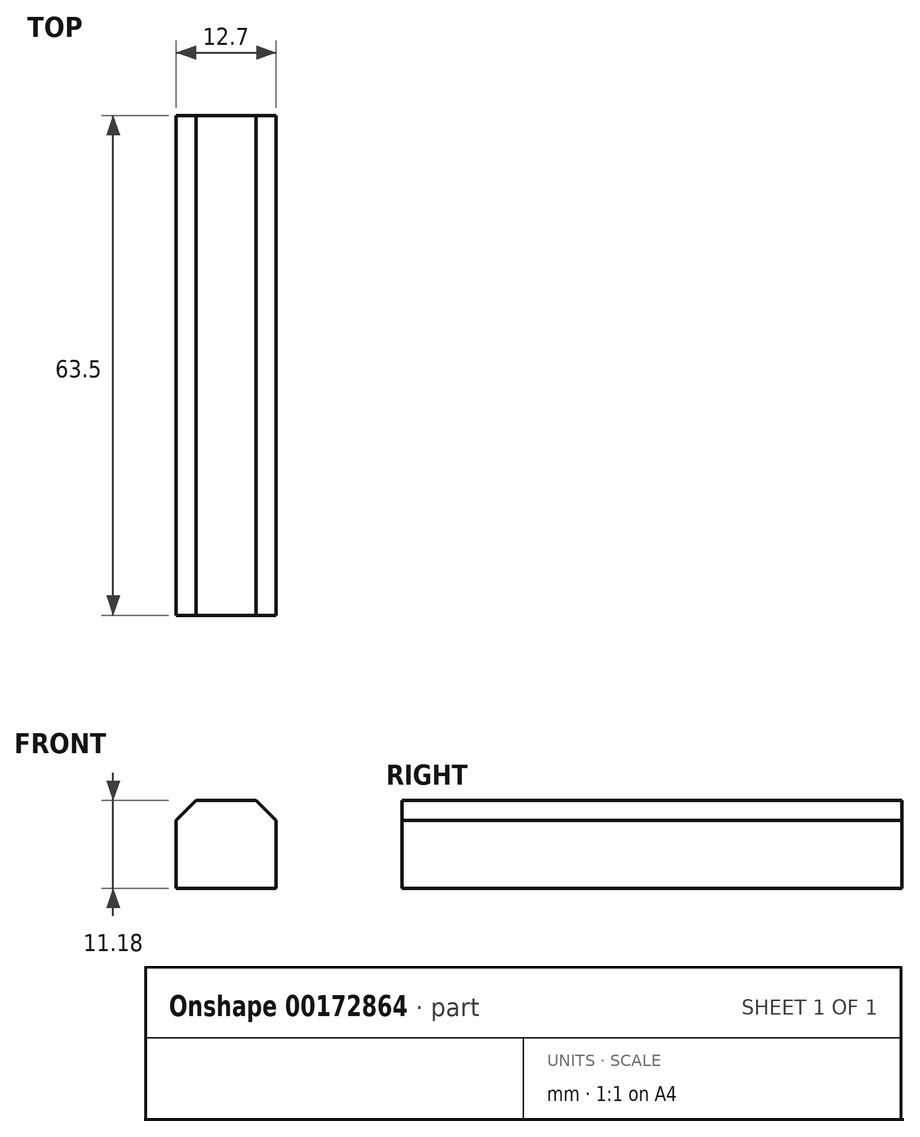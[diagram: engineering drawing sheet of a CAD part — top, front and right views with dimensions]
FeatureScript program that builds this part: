
annotation { "Feature Type Name" : "Feature", "Feature Type Description" : "" }
export const myFeature = defineFeature(function(context is Context, id is Id, definition is map)
    precondition{}
    {
        {
            var Q0;
            Q0=qCreatedBy(makeId("Top.planeOp"),FACE);
            var sketch = newSketch(context, id + "F0", { "sketchPlane" : qUnion([Q0])});
            skLineSegment(sketch, "E0.bottom", {"start": v(6.07, 24.83) * mm, "end": v(18.77, 24.83) * mm});
            skLineSegment(sketch, "E0.top", {"start": v(6.07, -38.67) * mm, "end": v(18.77, -38.67) * mm});
            skLineSegment(sketch, "E0.left", {"start": v(6.07, 24.83) * mm, "end": v(6.07, -38.67) * mm});
            skLineSegment(sketch, "E0.right", {"start": v(18.77, 24.83) * mm, "end": v(18.77, -38.67) * mm});
            skSolve(sketch);
        }
        {
            var Q0;
            Q0 = qSketchRegion(id + "F0", true);
            extrude(context, id + "F1", {"entities" : qUnion([Q0]), "depth" : 11.18 * mm});
        }
        {
            var Q0;
            Q0=makeQuery(id+"F1.opExtrude","CAP_EDGE",EDGE,{"disambiguationData":[OSD([sQuery(id+"F0.wireOp",EDGE,"E0.left")])],"isStart":false});
            var Q1;
            Q1=makeQuery(id+"F1.opExtrude","CAP_EDGE",EDGE,{"disambiguationData":[OSD([sQuery(id+"F0.wireOp",EDGE,"E0.right")])],"isStart":false});
            chamfer(context, id + "F2", {"entities" : qUnion([Q0, Q1]), "width" : 2.54 * mm, "tangentPropagation" : true});
        }
    });
